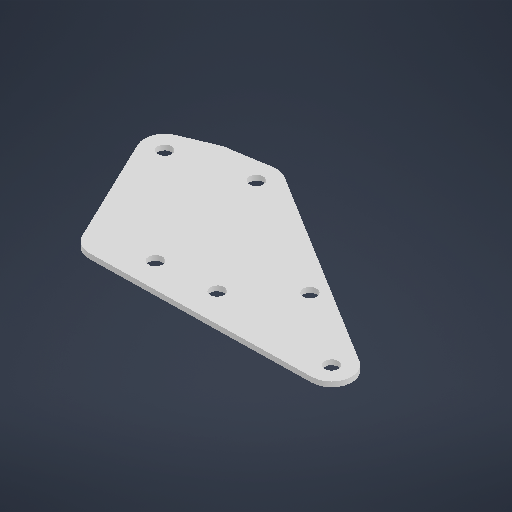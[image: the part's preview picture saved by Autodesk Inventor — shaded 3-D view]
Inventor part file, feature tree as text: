
AUTODESK INVENTOR PART (.ipt)
format: ipt  version: 2025.2 (Build 292293000, 293)  size: 205,824 bytes
history: native  units: in
note: dims shown in document units (in); Inventor stores cm internally (conversion verified against a paired STEP export)
features: extrude x1, sketch x1
ambient origin geometry x8: Origin, YZ Plane, XZ Plane, XY Plane, X Axis, Y Axis, Z Axis, Center Point
bodies: Solid1 (feature_tree)
feature tree (2):
  extrude  "Extrusion1"  Depth=0.0625in
  sketch  "Sketch1"  dims[d0=0.5in d1=0.5in d8=0.0625in d9=0.0in d10=0.5in d11=0.5in d12=0.5in d13=0.5in]
